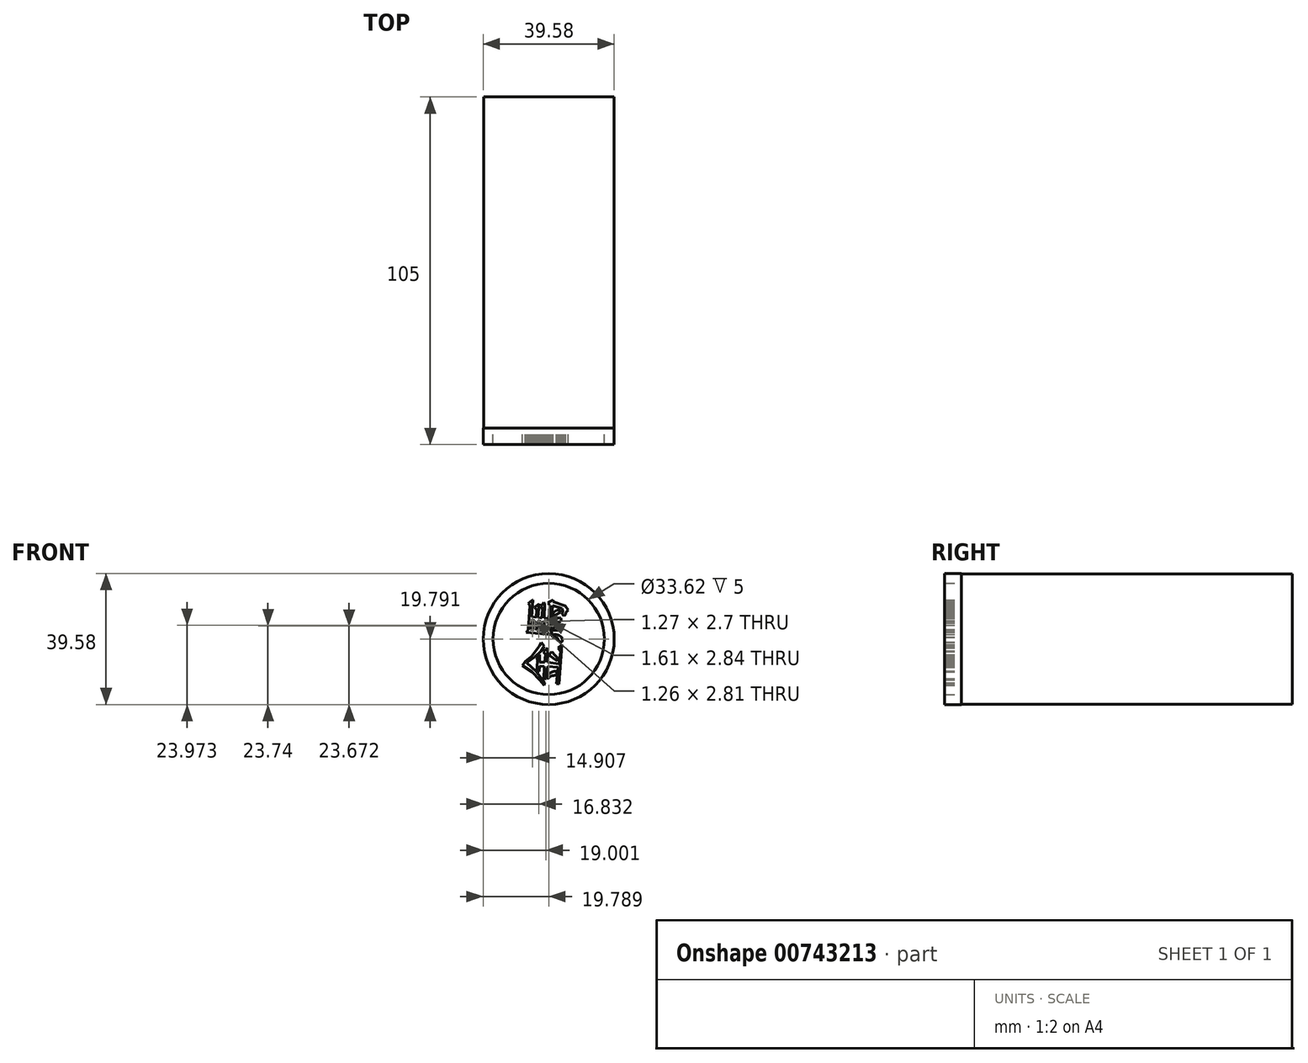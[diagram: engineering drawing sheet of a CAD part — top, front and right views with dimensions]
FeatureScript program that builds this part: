
annotation { "Feature Type Name" : "Feature", "Feature Type Description" : "" }
export const myFeature = defineFeature(function(context is Context, id is Id, definition is map)
    precondition{}
    {
        {
            var Q0;
            Q0=qCreatedBy(makeId("Front.planeOp"),FACE);
            var sketch = newSketch(context, id + "F0", { "sketchPlane" : qUnion([Q0])});
            skLineSegment(sketch, "E0", {"start": v(-37.3, 19.05) * mm, "end": v(-38.75, 20.7) * mm});
            skLineSegment(sketch, "E1", {"start": v(-38.75, 20.7) * mm, "end": v(-40.96, 23.12) * mm});
            skLineSegment(sketch, "E2", {"start": v(-40.96, 23.12) * mm, "end": v(-43.86, 24.98) * mm});
            skLineSegment(sketch, "E3", {"start": v(-43.86, 24.98) * mm, "end": v(-43.03, 26.27) * mm});
            skLineSegment(sketch, "E4", {"start": v(-43.03, 26.27) * mm, "end": v(-41.11, 27.8) * mm});
            skLineSegment(sketch, "E5", {"start": v(-41.11, 27.8) * mm, "end": v(-38.78, 30.83) * mm});
            skLineSegment(sketch, "E6", {"start": v(-38.78, 30.83) * mm, "end": v(-38.18, 31.97) * mm});
            skLineSegment(sketch, "E7", {"start": v(-38.18, 31.97) * mm, "end": v(-37.29, 30.88) * mm});
            skLineSegment(sketch, "E8", {"start": v(-37.29, 30.88) * mm, "end": v(-38.18, 29.4) * mm});
            skLineSegment(sketch, "E9", {"start": v(-38.18, 29.4) * mm, "end": v(-40.12, 27.65) * mm});
            skLineSegment(sketch, "E10", {"start": v(-40.12, 27.65) * mm, "end": v(-42.6, 25.87) * mm});
            skLineSegment(sketch, "E11", {"start": v(-42.6, 25.87) * mm, "end": v(-39.72, 23.23) * mm});
            skLineSegment(sketch, "E12", {"start": v(-39.72, 23.23) * mm, "end": v(-37.14, 19.76) * mm});
            skLineSegment(sketch, "E13", {"start": v(-37.14, 19.76) * mm, "end": v(-37.3, 19.05) * mm});
            skLineSegment(sketch, "E14", {"start": v(-39.6, 23.4) * mm, "end": v(-39.39, 26.3) * mm});
            skLineSegment(sketch, "E15", {"start": v(-39.39, 26.3) * mm, "end": v(-39.39, 26.75) * mm});
            skLineSegment(sketch, "E16", {"start": v(-39.39, 26.75) * mm, "end": v(-39.7, 27.31) * mm});
            skLineSegment(sketch, "E17", {"start": v(-39.7, 27.31) * mm, "end": v(-38.64, 28.3) * mm});
            skLineSegment(sketch, "E18", {"start": v(-38.64, 28.3) * mm, "end": v(-38.64, 26.04) * mm});
            skLineSegment(sketch, "E19", {"start": v(-38.64, 26.04) * mm, "end": v(-37.2, 26.04) * mm});
            skLineSegment(sketch, "E20", {"start": v(-37.2, 26.04) * mm, "end": v(-36.96, 28.3) * mm});
            skLineSegment(sketch, "E21", {"start": v(-36.96, 28.3) * mm, "end": v(-37.6, 29.14) * mm});
            skLineSegment(sketch, "E22", {"start": v(-37.6, 29.14) * mm, "end": v(-36.35, 30.28) * mm});
            skLineSegment(sketch, "E23", {"start": v(-36.35, 30.28) * mm, "end": v(-36.35, 25.97) * mm});
            skLineSegment(sketch, "E24", {"start": v(-36.35, 25.97) * mm, "end": v(-32.87, 25.54) * mm});
            skLineSegment(sketch, "E25", {"start": v(-32.87, 25.54) * mm, "end": v(-32.41, 29.22) * mm});
            skLineSegment(sketch, "E26", {"start": v(-32.41, 29.22) * mm, "end": v(-33.15, 30.28) * mm});
            skLineSegment(sketch, "E27", {"start": v(-33.15, 30.28) * mm, "end": v(-31.93, 31.35) * mm});
            skLineSegment(sketch, "E28", {"start": v(-31.93, 31.35) * mm, "end": v(-32.84, 19.45) * mm});
            skLineSegment(sketch, "E29", {"start": v(-32.84, 19.45) * mm, "end": v(-33.58, 19.51) * mm});
            skLineSegment(sketch, "E30", {"start": v(-33.58, 19.51) * mm, "end": v(-33.15, 24.54) * mm});
            skLineSegment(sketch, "E31", {"start": v(-33.15, 24.54) * mm, "end": v(-36.33, 24.82) * mm});
            skLineSegment(sketch, "E32", {"start": v(-36.33, 24.82) * mm, "end": v(-36.85, 21.1) * mm});
            skLineSegment(sketch, "E33", {"start": v(-36.85, 21.1) * mm, "end": v(-37.46, 21) * mm});
            skLineSegment(sketch, "E34", {"start": v(-37.46, 21) * mm, "end": v(-37.26, 24.74) * mm});
            skLineSegment(sketch, "E35", {"start": v(-37.26, 24.74) * mm, "end": v(-38.64, 24.93) * mm});
            skLineSegment(sketch, "E36", {"start": v(-38.64, 24.93) * mm, "end": v(-38.88, 23.24) * mm});
            skLineSegment(sketch, "E37", {"start": v(-38.88, 23.24) * mm, "end": v(-39.6, 23.4) * mm});
            skFitSpline(sketch, "E38", {"points": [v(-33.63, 23.09) * mm, v(-34.8, 23.13) * mm, v(-36.51, 21.56) * mm, v(-36.2, 21.14) * mm, v(-35.1, 21.91) * mm, v(-33.7, 22.18) * mm, v(-33.63, 23.09) * mm]});
            skLineSegment(sketch, "E39", {"start": v(-35.06, 29.23) * mm, "end": v(-35.95, 28.25) * mm});
            skLineSegment(sketch, "E40", {"start": v(-35.95, 28.25) * mm, "end": v(-33.4, 26.37) * mm});
            skLineSegment(sketch, "E41", {"start": v(-33.4, 26.37) * mm, "end": v(-33.04, 26.86) * mm});
            skLineSegment(sketch, "E42", {"start": v(-33.04, 26.86) * mm, "end": v(-35.06, 29.23) * mm});
            skFitSpline(sketch, "E43", {"points": [v(-32.88, 41.83) * mm, v(-34.59, 40.91) * mm, v(-34.85, 39.91) * mm, v(-33.71, 40.43) * mm, v(-32.93, 40.87) * mm, v(-32.4, 41.35) * mm, v(-32.88, 41.83) * mm]});
            skFitSpline(sketch, "E44", {"points": [v(-32.4, 39.34) * mm, v(-34.76, 38.47) * mm, v(-34.37, 37.86) * mm, v(-33.5, 38.25) * mm, v(-32.4, 38.3) * mm, v(-32.4, 39.34) * mm]});
            skFitSpline(sketch, "E45", {"points": [v(-31.93, 36.99) * mm, v(-34.06, 36.64) * mm, v(-34.98, 35.72) * mm, v(-33.63, 35.68) * mm, v(-31.93, 35.81) * mm, v(-31.93, 36.99) * mm]});
            skFitSpline(sketch, "E46", {"points": [v(-31.93, 33.24) * mm, v(-33.28, 34.29) * mm, v(-34.9, 34.11) * mm, v(-34.63, 33.59) * mm, v(-33.5, 33.54) * mm, v(-32.88, 32.45) * mm, v(-31.93, 32.28) * mm, v(-31.93, 33.24) * mm]});
            skLineSegment(sketch, "E47", {"start": v(-42.17, 35.8) * mm, "end": v(-41.58, 43.15) * mm});
            skLineSegment(sketch, "E48", {"start": v(-41.58, 43.15) * mm, "end": v(-42.1, 43.74) * mm});
            skLineSegment(sketch, "E49", {"start": v(-42.1, 43.74) * mm, "end": v(-40.9, 44.77) * mm});
            skLineSegment(sketch, "E50", {"start": v(-42.17, 35.8) * mm, "end": v(-42.75, 34.98) * mm});
            skLineSegment(sketch, "E51", {"start": v(-42.75, 34.98) * mm, "end": v(-40.35, 34.8) * mm});
            skLineSegment(sketch, "E52", {"start": v(-40.35, 34.8) * mm, "end": v(-35.62, 34.41) * mm});
            skLineSegment(sketch, "E53", {"start": v(-35.62, 34.41) * mm, "end": v(-34.9, 34.41) * mm});
            skLineSegment(sketch, "E54", {"start": v(-34.9, 34.41) * mm, "end": v(-35.12, 35.14) * mm});
            skLineSegment(sketch, "E55", {"start": v(-35.12, 35.14) * mm, "end": v(-35.4, 35.39) * mm});
            skLineSegment(sketch, "E56", {"start": v(-35.4, 35.39) * mm, "end": v(-34.78, 43.15) * mm});
            skLineSegment(sketch, "E57", {"start": v(-34.78, 43.15) * mm, "end": v(-32, 42.26) * mm});
            skLineSegment(sketch, "E58", {"start": v(-32, 42.26) * mm, "end": v(-31.75, 41.52) * mm});
            skLineSegment(sketch, "E59", {"start": v(-31.75, 41.52) * mm, "end": v(-31.83, 40.48) * mm});
            skLineSegment(sketch, "E60", {"start": v(-31.83, 40.48) * mm, "end": v(-31.3, 40) * mm});
            skLineSegment(sketch, "E61", {"start": v(-31.3, 40) * mm, "end": v(-30.89, 40.46) * mm});
            skLineSegment(sketch, "E62", {"start": v(-30.89, 40.46) * mm, "end": v(-30.77, 41.03) * mm});
            skLineSegment(sketch, "E63", {"start": v(-30.77, 41.03) * mm, "end": v(-30.1, 41.79) * mm});
            skLineSegment(sketch, "E64", {"start": v(-30.1, 41.79) * mm, "end": v(-30.97, 43.04) * mm});
            skLineSegment(sketch, "E65", {"start": v(-30.97, 43.04) * mm, "end": v(-34.67, 44.29) * mm});
            skLineSegment(sketch, "E66", {"start": v(-34.67, 44.29) * mm, "end": v(-34.67, 44.82) * mm});
            skLineSegment(sketch, "E67", {"start": v(-34.67, 44.82) * mm, "end": v(-35.85, 44.18) * mm});
            skLineSegment(sketch, "E68", {"start": v(-35.85, 44.18) * mm, "end": v(-36.19, 43.9) * mm});
            skLineSegment(sketch, "E69", {"start": v(-36.19, 43.9) * mm, "end": v(-35.62, 43.2) * mm});
            skLineSegment(sketch, "E70", {"start": v(-35.62, 43.2) * mm, "end": v(-35.94, 39.27) * mm});
            skLineSegment(sketch, "E71", {"start": v(-35.94, 39.27) * mm, "end": v(-37.28, 39.37) * mm});
            skLineSegment(sketch, "E72", {"start": v(-37.28, 39.37) * mm, "end": v(-37.13, 43.77) * mm});
            skLineSegment(sketch, "E73", {"start": v(-37.13, 43.77) * mm, "end": v(-37.48, 44.02) * mm});
            skLineSegment(sketch, "E74", {"start": v(-37.48, 44.02) * mm, "end": v(-38.26, 42.9) * mm});
            skLineSegment(sketch, "E75", {"start": v(-38.26, 42.9) * mm, "end": v(-37.86, 42.06) * mm});
            skLineSegment(sketch, "E76", {"start": v(-37.86, 42.06) * mm, "end": v(-38.07, 39.4) * mm});
            skLineSegment(sketch, "E77", {"start": v(-38.07, 39.4) * mm, "end": v(-39.16, 39.5) * mm});
            skLineSegment(sketch, "E78", {"start": v(-39.16, 39.5) * mm, "end": v(-38.82, 43.7) * mm});
            skLineSegment(sketch, "E79", {"start": v(-38.82, 43.7) * mm, "end": v(-40.2, 42.7) * mm});
            skLineSegment(sketch, "E80", {"start": v(-40.2, 42.7) * mm, "end": v(-39.54, 41.78) * mm});
            skLineSegment(sketch, "E81", {"start": v(-39.54, 41.78) * mm, "end": v(-39.7, 39.66) * mm});
            skLineSegment(sketch, "E82", {"start": v(-39.7, 39.66) * mm, "end": v(-41.1, 39.77) * mm});
            skLineSegment(sketch, "E83", {"start": v(-41.1, 39.77) * mm, "end": v(-40.7, 44.77) * mm});
            skLineSegment(sketch, "E84", {"start": v(-40.7, 44.77) * mm, "end": v(-40.9, 44.77) * mm});
            skLineSegment(sketch, "E85", {"start": v(-41.23, 38.62) * mm, "end": v(-40.2, 38.54) * mm});
            skLineSegment(sketch, "E86", {"start": v(-40.2, 38.54) * mm, "end": v(-40.42, 35.8) * mm});
            skLineSegment(sketch, "E87", {"start": v(-40.42, 35.8) * mm, "end": v(-41.46, 35.89) * mm});
            skLineSegment(sketch, "E88", {"start": v(-41.46, 35.89) * mm, "end": v(-41.23, 38.62) * mm});
            skLineSegment(sketch, "E89", {"start": v(-39.33, 38.33) * mm, "end": v(-39.54, 35.72) * mm});
            skLineSegment(sketch, "E90", {"start": v(-39.54, 35.72) * mm, "end": v(-38.49, 35.63) * mm});
            skLineSegment(sketch, "E91", {"start": v(-38.49, 35.63) * mm, "end": v(-38.27, 38.33) * mm});
            skLineSegment(sketch, "E92", {"start": v(-38.27, 38.33) * mm, "end": v(-39.33, 38.33) * mm});
            skLineSegment(sketch, "E93", {"start": v(-37.33, 38.33) * mm, "end": v(-37.55, 35.6) * mm});
            skLineSegment(sketch, "E94", {"start": v(-37.55, 35.6) * mm, "end": v(-36.15, 35.5) * mm});
            skLineSegment(sketch, "E95", {"start": v(-36.15, 35.5) * mm, "end": v(-35.93, 38.15) * mm});
            skLineSegment(sketch, "E96", {"start": v(-35.93, 38.15) * mm, "end": v(-37.33, 38.33) * mm});
            skCircle(sketch, "E97", {"center": v(-35.95, 33.03) * mm, "radius": 19.79 * mm});
            skCircle(sketch, "E98", {"center": v(-35.95, 33.03) * mm, "radius": 16.8 * mm});
            skSolve(sketch);
        }
        {
            var Q0;
            Q0=makeQuery(id+"F0.imprint","IMPRINT",FACE,{"disambiguationData":[TD([[makeQuery(id+"F0.imprint","IMPRINT",EDGE,{"derivedFrom":sQuery(id+"F0.wireOp",EDGE,"E47")}),-1.0]])]});
            var Q1;
            Q1=makeQuery(id+"F0.imprint","IMPRINT",FACE,{"disambiguationData":[TD([[makeQuery(id+"F0.imprint","IMPRINT",EDGE,{"derivedFrom":sQuery(id+"F0.wireOp",EDGE,"E43")}),1.0]])]});
            var Q2;
            Q2=makeQuery(id+"F0.imprint","IMPRINT",FACE,{"disambiguationData":[TD([[makeQuery(id+"F0.imprint","IMPRINT",EDGE,{"derivedFrom":sQuery(id+"F0.wireOp",EDGE,"E44")}),1.0]])]});
            var Q3;
            Q3=makeQuery(id+"F0.imprint","IMPRINT",FACE,{"disambiguationData":[TD([[makeQuery(id+"F0.imprint","IMPRINT",EDGE,{"derivedFrom":sQuery(id+"F0.wireOp",EDGE,"E45")}),1.0]])]});
            var Q4;
            Q4=makeQuery(id+"F0.imprint","IMPRINT",FACE,{"disambiguationData":[TD([[makeQuery(id+"F0.imprint","IMPRINT",EDGE,{"derivedFrom":sQuery(id+"F0.wireOp",EDGE,"E46")}),1.0]])]});
            var Q5;
            Q5=makeQuery(id+"F0.imprint","IMPRINT",FACE,{"disambiguationData":[TD([[makeQuery(id+"F0.imprint","IMPRINT",EDGE,{"derivedFrom":sQuery(id+"F0.wireOp",EDGE,"E0")}),-1.0]])]});
            var Q6;
            Q6=makeQuery(id+"F0.imprint","IMPRINT",FACE,{"disambiguationData":[TD([[makeQuery(id+"F0.imprint","IMPRINT",EDGE,{"derivedFrom":sQuery(id+"F0.wireOp",EDGE,"E14")}),-1.0]])]});
            var Q7;
            Q7=makeQuery(id+"F0.imprint","IMPRINT",FACE,{"disambiguationData":[TD([[makeQuery(id+"F0.imprint","IMPRINT",EDGE,{"derivedFrom":sQuery(id+"F0.wireOp",EDGE,"E38")}),1.0]])]});
            var Q8;
            Q8=makeQuery(id+"F0.imprint","IMPRINT",FACE,{"disambiguationData":[TD([[makeQuery(id+"F0.imprint","IMPRINT",EDGE,{"derivedFrom":sQuery(id+"F0.wireOp",EDGE,"E39")}),1.0]])]});
            extrude(context, id + "F1", {"entities" : qUnion([Q0, Q1, Q2, Q3, Q4, Q5, Q6, Q7, Q8]), "depth" : 5 * mm, "offsetDistance" : 25 * mm});
        }
        {
            var Q0;
            Q0=makeQuery(id+"F0.imprint","IMPRINT",FACE,{"disambiguationData":[TD([[makeQuery(id+"F0.imprint","IMPRINT",EDGE,{"derivedFrom":sQuery(id+"F0.wireOp",EDGE,"E47")}),-1.0]])]});
            var sketch = newSketch(context, id + "F2", { "sketchPlane" : qUnion([Q0])});
            skCircle(sketch, "E99", {"center": v(-35.96, 33.03) * mm, "radius": 19.67 * mm});
            skSolve(sketch);
        }
        {
            var Q0;
            Q0 = qSketchRegion(id + "F2", true);
            extrude(context, id + "F3", {"entities" : qUnion([Q0]), "oppositeDirection" : true, "depth" : 100 * mm, "offsetDistance" : 25 * mm});
        }
        {
            var Q0;
            Q0=makeQuery(id+"F0.imprint","IMPRINT",FACE,{"disambiguationData":[TD([[makeQuery(id+"F0.imprint","IMPRINT",EDGE,{"derivedFrom":sQuery(id+"F0.wireOp",EDGE,"E97")}),1.0]])]});
            extrude(context, id + "F4", {"entities" : qUnion([Q0]), "operationType" : NewBodyOperationType.ADD, "depth" : 5 * mm, "offsetDistance" : 25 * mm});
        }
    });
